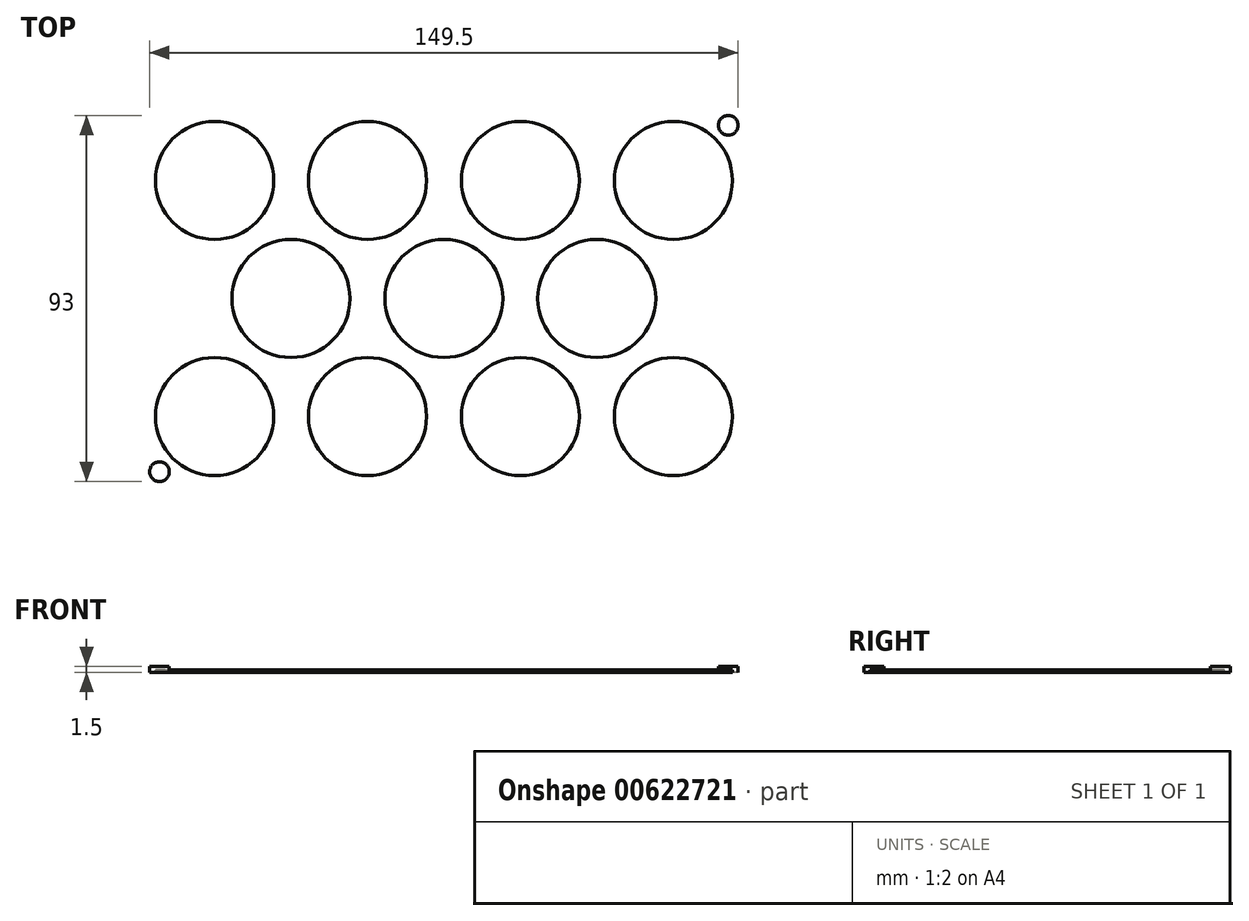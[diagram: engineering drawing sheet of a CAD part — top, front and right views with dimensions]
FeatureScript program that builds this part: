
annotation { "Feature Type Name" : "Feature", "Feature Type Description" : "" }
export const myFeature = defineFeature(function(context is Context, id is Id, definition is map)
    precondition{}
    {
        {
            var Q0;
            Q0=qCreatedBy(makeId("Top.planeOp"),FACE);
            var sketch = newSketch(context, id + "F0", { "sketchPlane" : qUnion([Q0])});
            skLineSegment(sketch, "E0.bottom", {"start": v(-76.25, 48) * mm, "end": v(76.25, 48) * mm});
            skLineSegment(sketch, "E0.top", {"start": v(-76.25, -48) * mm, "end": v(76.25, -48) * mm});
            skLineSegment(sketch, "E0.left", {"start": v(-76.25, 48) * mm, "end": v(-76.25, -48) * mm});
            skLineSegment(sketch, "E0.right", {"start": v(76.25, 48) * mm, "end": v(76.25, -48) * mm});
            skPoint(sketch, "E0.middle", {"position": v(0, 0) * mm});
            skCircle(sketch, "E1", {"center": v(-58.25, 30) * mm, "radius": 15 * mm});
            skCircle(sketch, "E2.1.0.0", {"center": v(-19.4, 30) * mm, "radius": 15 * mm});
            skCircle(sketch, "E2.2.0.0", {"center": v(19.45, 30) * mm, "radius": 15 * mm});
            skCircle(sketch, "E2.3.0.0", {"center": v(58.3, 30) * mm, "radius": 15 * mm});
            skLineSegment(sketch, "E2.direction1", {"start": v(-58.25, 30) * mm, "end": v(-19.4, 30) * mm, "construction": true});
            skLineSegment(sketch, "E2.direction2", {"start": v(-58.25, 30) * mm, "end": v(-58.25, 0) * mm, "construction": true});
            skCircle(sketch, "E3", {"center": v(0, 0) * mm, "radius": 15 * mm});
            skCircle(sketch, "E4", {"center": v(-38.85, 0) * mm, "radius": 15 * mm});
            skCircle(sketch, "E5", {"center": v(38.85, 0) * mm, "radius": 15 * mm});
            skCircle(sketch, "E6", {"center": v(-58.25, -30) * mm, "radius": 15 * mm});
            skPoint(sketch, "E6.centerSnap0", {"position": v(-58.25, 15) * mm});
            skCircle(sketch, "E7.1.0.0", {"center": v(-19.4, -30) * mm, "radius": 15 * mm});
            skCircle(sketch, "E7.2.0.0", {"center": v(19.45, -30) * mm, "radius": 15 * mm});
            skCircle(sketch, "E7.3.0.0", {"center": v(58.3, -30) * mm, "radius": 15 * mm});
            skLineSegment(sketch, "E7.direction1", {"start": v(-58.25, -30) * mm, "end": v(-19.4, -30) * mm, "construction": true});
            skSolve(sketch);
        }
        {
            var Q0;
            Q0=qSketchRegion(id+"F0",true);
            extrude(context, id + "F1", {"entities" : qUnion([Q0]), "depth" : 0.9 * mm, "offsetDistance" : 25 * mm});
        }
        {
            var Q0;
            Q0 = qSketchRegion(id + "F0", true);
            var Q1;
            Q1=makeQuery(id+"F0.imprint","IMPRINT",FACE,{"disambiguationData":[TD([[makeQuery(id+"F0.imprint","IMPRINT",EDGE,{"derivedFrom":sQuery(id+"F0.wireOp",EDGE,"E6")}),1.0]])]});
            var Q2;
            Q2=makeQuery(id+"F0.imprint","IMPRINT",FACE,{"disambiguationData":[TD([[makeQuery(id+"F0.imprint","IMPRINT",EDGE,{"derivedFrom":sQuery(id+"F0.wireOp",EDGE,"E4")}),1.0]])]});
            var Q3;
            Q3=makeQuery(id+"F0.imprint","IMPRINT",FACE,{"disambiguationData":[TD([[makeQuery(id+"F0.imprint","IMPRINT",EDGE,{"derivedFrom":sQuery(id+"F0.wireOp",EDGE,"E1")}),1.0]])]});
            var Q4;
            Q4=makeQuery(id+"F0.imprint","IMPRINT",FACE,{"disambiguationData":[TD([[makeQuery(id+"F0.imprint","IMPRINT",EDGE,{"derivedFrom":sQuery(id+"F0.wireOp",EDGE,"E2.1.0.0")}),1.0]])]});
            var Q5;
            Q5=makeQuery(id+"F0.imprint","IMPRINT",FACE,{"disambiguationData":[TD([[makeQuery(id+"F0.imprint","IMPRINT",EDGE,{"derivedFrom":sQuery(id+"F0.wireOp",EDGE,"E2.2.0.0")}),1.0]])]});
            var Q6;
            Q6=makeQuery(id+"F0.imprint","IMPRINT",FACE,{"disambiguationData":[TD([[makeQuery(id+"F0.imprint","IMPRINT",EDGE,{"derivedFrom":sQuery(id+"F0.wireOp",EDGE,"E3")}),1.0]])]});
            var Q7;
            Q7=makeQuery(id+"F0.imprint","IMPRINT",FACE,{"disambiguationData":[TD([[makeQuery(id+"F0.imprint","IMPRINT",EDGE,{"derivedFrom":sQuery(id+"F0.wireOp",EDGE,"E5")}),1.0]])]});
            var Q8;
            Q8=makeQuery(id+"F0.imprint","IMPRINT",FACE,{"disambiguationData":[TD([[makeQuery(id+"F0.imprint","IMPRINT",EDGE,{"derivedFrom":sQuery(id+"F0.wireOp",EDGE,"E7.2.0.0")}),1.0]])]});
            var Q9;
            Q9=makeQuery(id+"F0.imprint","IMPRINT",FACE,{"disambiguationData":[TD([[makeQuery(id+"F0.imprint","IMPRINT",EDGE,{"derivedFrom":sQuery(id+"F0.wireOp",EDGE,"E7.3.0.0")}),1.0]])]});
            var Q10;
            Q10=makeQuery(id+"F0.imprint","IMPRINT",FACE,{"disambiguationData":[TD([[makeQuery(id+"F0.imprint","IMPRINT",EDGE,{"derivedFrom":sQuery(id+"F0.wireOp",EDGE,"E2.3.0.0")}),1.0]])]});
            var Q11;
            Q11=makeQuery(id+"F0.imprint","IMPRINT",FACE,{"disambiguationData":[TD([[makeQuery(id+"F0.imprint","IMPRINT",EDGE,{"derivedFrom":sQuery(id+"F0.wireOp",EDGE,"E7.1.0.0")}),1.0]])]});
            extrude(context, id + "F2", {"entities" : qUnion([Q0, Q1, Q2, Q3, Q4, Q5, Q6, Q7, Q8, Q9, Q10, Q11]), "operationType" : NewBodyOperationType.ADD, "oppositeDirection" : true, "depth" : 0.6 * mm, "offsetDistance" : 25 * mm});
        }
        {
            var Q0;
            Q0=makeQuery(id+"F1.opExtrude","CAP_FACE",FACE,{"disambiguationData":[OSD([sQuery(id+"F0.wireOp",EDGE,"E0.bottom"),sQuery(id+"F0.wireOp",EDGE,"E0.top"),sQuery(id+"F0.wireOp",EDGE,"E0.left"),sQuery(id+"F0.wireOp",EDGE,"E0.right"),sQuery(id+"F0.wireOp",EDGE,"E1"),sQuery(id+"F0.wireOp",EDGE,"E2.0.1.0"),sQuery(id+"F0.wireOp",EDGE,"E2.0.2.0"),sQuery(id+"F0.wireOp",EDGE,"E2.0.3.0"),sQuery(id+"F0.wireOp",EDGE,"E2.0.4.0"),sQuery(id+"F0.wireOp",EDGE,"E2.1.0.0"),sQuery(id+"F0.wireOp",EDGE,"E2.1.1.0"),sQuery(id+"F0.wireOp",EDGE,"E2.1.2.0"),sQuery(id+"F0.wireOp",EDGE,"E2.1.3.0"),sQuery(id+"F0.wireOp",EDGE,"E2.1.4.0"),sQuery(id+"F0.wireOp",EDGE,"E2.2.0.0"),sQuery(id+"F0.wireOp",EDGE,"E2.2.1.0"),sQuery(id+"F0.wireOp",EDGE,"E2.2.2.0"),sQuery(id+"F0.wireOp",EDGE,"E2.2.3.0"),sQuery(id+"F0.wireOp",EDGE,"E2.2.4.0"),sQuery(id+"F0.wireOp",EDGE,"E2.3.0.0"),sQuery(id+"F0.wireOp",EDGE,"E2.3.1.0"),sQuery(id+"F0.wireOp",EDGE,"E2.3.2.0"),sQuery(id+"F0.wireOp",EDGE,"E2.3.3.0"),sQuery(id+"F0.wireOp",EDGE,"E2.3.4.0"),sQuery(id+"F0.wireOp",EDGE,"E2.4.0.0"),sQuery(id+"F0.wireOp",EDGE,"E2.4.1.0"),sQuery(id+"F0.wireOp",EDGE,"E2.4.2.0"),sQuery(id+"F0.wireOp",EDGE,"E2.4.3.0"),sQuery(id+"F0.wireOp",EDGE,"E2.4.4.0")])],"isStart":false});
            var sketch = newSketch(context, id + "F3", { "sketchPlane" : qUnion([Q0])});
            skLineSegment(sketch, "E8", {"start": v(0, 78.4) * mm, "end": v(0, -88.75) * mm, "construction": true});
            skLineSegment(sketch, "E9", {"start": v(-112.04, 0) * mm, "end": v(125.52, 0) * mm, "construction": true});
            skCircle(sketch, "E10", {"center": v(-72.25, 44) * mm, "radius": 2.5 * mm});
            skCircle(sketch, "E11.MirrorC", {"center": v(-72.25, -44) * mm, "radius": 2.5 * mm});
            skCircle(sketch, "E12.MirrorC", {"center": v(72.25, 44) * mm, "radius": 2.5 * mm});
            skCircle(sketch, "E13.MirrorC", {"center": v(72.25, -44) * mm, "radius": 2.5 * mm});
            skCircle(sketch, "E14", {"center": v(-19.43, 0) * mm, "radius": 2.5 * mm});
            skCircle(sketch, "E15", {"center": v(19.42, 0) * mm, "radius": 2.5 * mm});
            skSolve(sketch);
        }
        {
            var Q0;
            Q0=makeQuery(id+"F3.imprint","IMPRINT",FACE,{"disambiguationData":[TD([[makeQuery(id+"F3.imprint","IMPRINT",EDGE,{"derivedFrom":sQuery(id+"F3.wireOp",EDGE,"E10")}),1.0]])]});
            var Q1;
            Q1=makeQuery(id+"F3.imprint","IMPRINT",FACE,{"disambiguationData":[TD([[makeQuery(id+"F3.imprint","IMPRINT",EDGE,{"derivedFrom":sQuery(id+"F3.wireOp",EDGE,"sxCIsY3Z-BQGj-H5cd-ML4T-SCUDd1a1iyz5")}),1.0]])]});
            var Q2;
            Q2=makeQuery(id+"F3.imprint","IMPRINT",FACE,{"disambiguationData":[TD([[makeQuery(id+"F3.imprint","IMPRINT",EDGE,{"derivedFrom":sQuery(id+"F3.wireOp",EDGE,"d9ea3425-a531-48dc-9db2-9a486e82fd170.MirrorC")}),-1.0]])]});
            var Q3;
            Q3=makeQuery(id+"F3.imprint","IMPRINT",FACE,{"disambiguationData":[TD([[makeQuery(id+"F3.imprint","IMPRINT",EDGE,{"derivedFrom":sQuery(id+"F3.wireOp",EDGE,"E12.MirrorC")}),-1.0]])]});
            var Q4;
            Q4=makeQuery(id+"F3.imprint","IMPRINT",FACE,{"disambiguationData":[TD([[makeQuery(id+"F3.imprint","IMPRINT",EDGE,{"derivedFrom":sQuery(id+"F3.wireOp",EDGE,"46409f2a-6570-4a76-ac75-4a490cd369680.MirrorC")}),1.0]])]});
            var Q5;
            Q5=makeQuery(id+"F3.imprint","IMPRINT",FACE,{"disambiguationData":[TD([[makeQuery(id+"F3.imprint","IMPRINT",EDGE,{"derivedFrom":sQuery(id+"F3.wireOp",EDGE,"ea06a8f7-23f5-47a6-a1bc-bac05f767e070.MirrorC")}),-1.0]])]});
            var Q6;
            Q6=makeQuery(id+"F3.imprint","IMPRINT",FACE,{"disambiguationData":[TD([[makeQuery(id+"F3.imprint","IMPRINT",EDGE,{"derivedFrom":sQuery(id+"F3.wireOp",EDGE,"E11.MirrorC")}),-1.0]])]});
            var Q7;
            Q7=makeQuery(id+"F3.imprint","IMPRINT",FACE,{"disambiguationData":[TD([[makeQuery(id+"F3.imprint","IMPRINT",EDGE,{"derivedFrom":sQuery(id+"F3.wireOp",EDGE,"E13.MirrorC")}),1.0]])]});
            var Q8;
            Q8=makeQuery(id+"F3.imprint","IMPRINT",FACE,{"disambiguationData":[TD([[makeQuery(id+"F3.imprint","IMPRINT",EDGE,{"derivedFrom":sQuery(id+"F3.wireOp",EDGE,"6qHL3Yw1-V7cY-TyVk-lXy9-OHWvkYreJjHo")}),1.0]])]});
            var Q9;
            Q9=makeQuery(id+"F3.imprint","IMPRINT",FACE,{"disambiguationData":[TD([[makeQuery(id+"F3.imprint","IMPRINT",EDGE,{"derivedFrom":sQuery(id+"F3.wireOp",EDGE,"LLc5zwvZ-dcbx-mEB2-hhTY-IF1h5IE9Gclt")}),1.0]])]});
            var Q10;
            Q10=makeQuery(id+"F3.imprint","IMPRINT",FACE,{"disambiguationData":[TD([[makeQuery(id+"F3.imprint","IMPRINT",EDGE,{"derivedFrom":sQuery(id+"F3.wireOp",EDGE,"E14")}),1.0]])]});
            var Q11;
            Q11=makeQuery(id+"F3.imprint","IMPRINT",FACE,{"disambiguationData":[TD([[makeQuery(id+"F3.imprint","IMPRINT",EDGE,{"derivedFrom":sQuery(id+"F3.wireOp",EDGE,"E15")}),1.0]])]});
            extrude(context, id + "F4", {"entities" : qUnion([Q0, Q1, Q2, Q3, Q4, Q5, Q6, Q7, Q8, Q9, Q10, Q11]), "operationType" : NewBodyOperationType.REMOVE, "endBound" : BoundingType.THROUGH_ALL, "oppositeDirection" : true, "depth" : 34 * mm, "offsetDistance" : 25 * mm});
        }
    });
